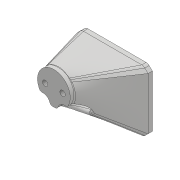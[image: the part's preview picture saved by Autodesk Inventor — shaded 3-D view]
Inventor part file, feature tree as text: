
AUTODESK INVENTOR PART (.ipt)
format: ipt  version: 2018 (Build 220112000, 112)  size: 1,732,096 bytes
history: native  units: mm
features: sketch x48, extrude x40, projected_geometry x39, fillet x13, hole x12, chamfer x10, plane x2, mirror x1, loft x1, other x1
ambient origin geometry x8: Origin, YZ Plane, XZ Plane, XY Plane, X Axis, Y Axis, Z Axis, Center Point
bodies: Solid1 (feature_tree), Solid2 (feature_tree)
feature tree (167):
  extrude  "Extrusion1"  Depth=45.0mm
  extrude  "Extrusion2"  Depth=2.25mm
  hole  "Hole1"  [1 undecoded]
  hole  "Hole2"  [1 undecoded]
  fillet  "Fillet1"  Radius=14.0mm
  extrude  "Extrusion3"  Depth=18.5mm
  extrude  "Extrusion4"  Depth=10.0mm
  extrude  "Extrusion5"  Depth=2.195mm
  extrude  "Extrusion6"  Depth=20.5mm
  hole  "Hole3"  [1 undecoded]
  extrude  "Extrusion7"  Depth=0.5mm
  extrude  "Extrusion8"  Depth=5.0mm TaperAngle=0.0deg
  extrude  "Extrusion9"  Depth=10.0mm
  extrude  "Extrusion10"  Depth=10.0mm
  extrude  "Extrusion11"  Depth=14.5mm
  extrude  "Extrusion12"  Depth=14.5mm
  extrude  "Extrusion13"  Depth=5.0mm
  extrude  "Extrusion14"  Depth=2.25mm
  extrude  "Extrusion15"  Depth=5.0mm
  extrude  "Extrusion16"  Depth=9.0mm
  extrude  "Extrusion17"  Depth=4.0mm
  chamfer  "Chamfer1"  Distance=1.0mm
  fillet  "Fillet7"  Radius=20.7mm
  fillet  "Fillet8"  Radius=32.0mm
  mirror  "Mirror1"
  extrude  "Extrusion19"  Depth=1.0mm TaperAngle=0.0deg
  extrude  "Extrusion20"  Depth=8.0mm
  extrude  "Extrusion21"  Depth=0.2mm TaperAngle=0.0deg
  extrude  "Extrusion22"  Depth=0.5mm TaperAngle=0.0deg
  sketch  "Sketch29"  dims[d77=12.25mm d78=0.0mm d80=8.0mm]
  extrude  "Extrusion23"  Depth=5.0mm TaperAngle=0.0deg
  extrude  "Extrusion24"  Depth=0.2mm TaperAngle=0.0deg
  plane  "Work Plane1"
  extrude  "Extrusion25"  Depth=2.5mm TaperAngle=45.0deg
  extrude  "Extrusion26"  Depth=0.5mm
  extrude  "Extrusion27"  Depth=8.0mm
  extrude  "Extrusion28"  Depth=3.0mm TaperAngle=0.0deg
  extrude  "Extrusion29"  Depth=33.0mm
  extrude  "Extrusion30"  Depth=56.0mm
  extrude  "Extrusion31"  Depth=25.0mm TaperAngle=0.0deg
  chamfer  "Chamfer2"  Distance=6.0mm
  hole  "Hole6"  [1 undecoded]
  chamfer  "Chamfer3"  Distance=40.0mm
  extrude  "Extrusion32"  Depth=12.0mm
  extrude  "Extrusion33"  Depth=40.0mm TaperAngle=0.0deg
  chamfer  "Chamfer4"  Distance=40.0mm
  chamfer  "Chamfer5"  Distance=1.8mm
  chamfer  "Chamfer6"  Distance=3.3mm
  fillet  "Fillet9"  Radius=14.0mm
  extrude  "Extrusion34"  Depth=1.2mm TaperAngle=45.0deg
  chamfer  "Chamfer7"  Distance=2.5mm
  sketch  "Sketch42"  dims[d146=6.0mm d147=0.0mm d149=42.0mm]
  hole  "Hole7"  [1 undecoded]
  hole  "Hole8"  [1 undecoded]
  hole  "Hole9"  [1 undecoded]
  fillet  "Fillet10"  Radius=3.0mm
  chamfer  "Chamfer8"  Distance=2.0mm
  chamfer  "Chamfer9"  Distance=12.0mm
  fillet  "Fillet11"  Radius=2.0mm
  fillet  "Fillet12"  Radius=15.0mm
  extrude  "Extrusion35"  Depth=10.0mm TaperAngle=0.0deg
  sketch  "Sketch45"  dims[d151=4.5mm]
  hole  "Hole10"  [1 undecoded]
  hole  "Hole11"  [1 undecoded]
  hole  "Hole12"  [1 undecoded]
  fillet  "Fillet13"  Radius=3.18mm
  fillet  "Fillet14"  Radius=3.18mm
  fillet  "Fillet15"  Radius=0.5mm
  chamfer  "Chamfer10"  Distance=2.0mm Angle=45.0deg
  extrude  "Extrusion36"  Depth=10.0mm TaperAngle=45.0deg
  sketch  "Sketch47"  dims[d155=28.0mm d156=12.0mm]
  extrude  "Extrusion37"  Depth=10.0mm
  extrude  "Extrusion38"  Depth=10.0mm
  plane  "Work Plane2"
  loft  "Loft1"
  hole  "Hole13"  [1 undecoded]
  extrude  "Extrusion39"  Depth=10.0mm TaperAngle=0.0deg
  extrude  "Extrusion40"  Depth=10.0mm
  fillet  "Fillet16"  Radius=2.75mm
  fillet  "Fillet17"  Radius=2.5mm
  extrude  "Extrusion41"  Depth=10.0mm
  fillet  "Fillet18"  Radius=2.0mm
  hole  "Hole14"  [1 undecoded]
  sketch  "Sketch1"  dims[d0=24.5mm d1=45.0mm]
  sketch  "Sketch2"  dims[d2=1.95mm d3=0.0mm d4=2.25mm]
  projected_geometry  "Projected Loop1"
  sketch  "Sketch3"  dims[d5=20.0mm d6=2.25mm]
  projected_geometry  "Projected Loop2"
  sketch  "Sketch4"  dims[d7=5.25mm d8=5.25mm d9=14.0mm]
  projected_geometry  "Projected Loop3"
  sketch  "Sketch5"  dims[d10=5.25mm d11=18.5mm]
  projected_geometry  "Projected Loop4"
  sketch  "Sketch6"  dims[d12=10.0mm d13=0.0mm d14=20.5mm]
  projected_geometry  "Projected Loop5"
  sketch  "Sketch7"  dims[d15=2.0mm d16=2.195mm]
  projected_geometry  "Projected Loop6"
  sketch  "Sketch8"  dims[d17=2.0mm]
  projected_geometry  "Projected Loop7"
  sketch  "Sketch9"  dims[d18=2.4mm d19=6.0mm d20=4.4mm d21=2.0mm d22=90.0deg d23=8.0mm d24=20.594885mm d25=20.5mm]
  projected_geometry  "Projected Loop8"
  projected_geometry  "Projected Loop9"
  sketch  "Sketch10"  dims[d26=26.65mm d27=2.0mm]
  projected_geometry  "Projected Loop10"
  projected_geometry  "Projected Loop11"
  sketch  "Sketch11"  dims[d28=2.0mm]
  projected_geometry  "Projected Loop12"
  sketch  "Sketch12"  dims[d29=2.4mm d30=6.0mm d31=4.4mm d32=2.0mm d33=90.0deg d34=8.0mm d35=20.594885mm d36=0.5mm]
  sketch  "Sketch13"  dims[d37=18.0mm d38=5.0mm d39=0.0mm]
  sketch  "Sketch14"  dims[d41=10.0mm d42=0.0mm d43=24.5mm]
  projected_geometry  "Projected Loop13"
  sketch  "Sketch15"  dims[d44=1.15mm d45=0.0mm d46=10.0mm]
  sketch  "Sketch16"  dims[d47=21.0mm d48=14.5mm]
  projected_geometry  "Projected Loop14"
  sketch  "Sketch17"  dims[d49=20.0mm d50=14.5mm]
  projected_geometry  "Projected Loop15"
  sketch  "Sketch18"  dims[d51=24.5mm d52=5.0mm]
  projected_geometry  "Projected Loop16"
  sketch  "Sketch19"  dims[d53=5.0mm d54=2.25mm]
  projected_geometry  "Projected Loop17"
  sketch  "Sketch20"  dims[d55=2.25mm d56=5.0mm]
  projected_geometry  "Projected Loop18"
  sketch  "Sketch25"  dims[d57=5.0mm d58=9.0mm]
  projected_geometry  "Projected Loop22"
  sketch  "Sketch26"  dims[d59=14.75mm d60=4.0mm d61=1.0mm d62=0.0mm d63=20.7mm]
  sketch  "Sketch27"  dims[d64=2.4mm d65=6.0mm d66=4.4mm d67=2.0mm d68=90.0deg d69=8.0mm d70=20.594885mm d72=32.0mm]
  projected_geometry  "Projected Loop23"
  sketch  "Sketch28"  dims[d73=5.0mm d74=0.0mm d75=1.0mm d76=0.0mm]
  projected_geometry  "Projected Loop24"
  sketch  "Sketch31"  dims[d81=4.5mm d82=0.0mm d84=0.2mm d85=0.0mm]
  projected_geometry  "Projected Loop25"
  sketch  "Sketch32"  dims[d86=21.0mm d87=0.5mm d88=0.0mm]
  projected_geometry  "Projected Loop26"
  sketch  "Sketch33"  dims[d91=8.0mm d92=0.0mm d93=5.0mm d94=0.0mm]
  sketch  "Sketch34"  dims[d95=5.0mm d96=0.0mm d98=0.2mm d99=0.0mm]
  sketch  "Sketch35"  dims[d100=0.2mm d101=0.0mm d102=2.5mm d103=2.0mm d104=45.0deg]
  projected_geometry  "Projected Loop27"
  sketch  "Sketch36"  dims[d105=1.5mm d114=0.5mm]
  sketch  "Sketch37"  dims[d128=4.0mm d129=0.0mm d130=8.0mm]
  sketch  "Sketch38"  dims[d131=3.0mm d132=0.0mm d133=3.0mm d134=0.0mm]
  projected_geometry  "Projected Loop28"
  sketch  "Sketch39"  dims[d135=25.0mm d136=0.0mm d137=33.0mm]
  projected_geometry  "Projected Loop29"
  sketch  "Sketch40"  dims[d138=2.5mm d139=56.0mm]
  projected_geometry  "Projected Loop30"
  sketch  "Sketch41"  dims[d140=25.0mm d141=0.0mm d142=25.0mm d143=0.0mm d144=6.0mm d145=0.0mm]
  sketch  "Sketch44"  dims[d150=4.5mm]
  projected_geometry  "Projected Loop31"
  projected_geometry  "Projected Loop32"
  projected_geometry  "Projected Loop33"
  sketch  "Sketch46"  dims[d152=4.5mm d153=40.0mm d154=0.0mm]
  projected_geometry  "Projected Loop34"
  sketch  "Sketch48"  dims[d157=12.0mm d158=40.0mm d159=0.0mm d160=40.0mm d161=0.0mm]
  projected_geometry  "Projected Loop35"
  sketch  "Sketch49"  dims[d162=20.5mm d163=1.8mm d164=0.0mm]
  other  "Edges1"
  sketch  "Sketch50"  dims[d165=20.5mm d166=3.3mm d167=0.0mm]
  projected_geometry  "Projected Loop36"
  sketch  "Sketch51"  dims[d168=2.0mm d169=2.0mm d170=45.0deg d171=14.0mm]
  projected_geometry  "Projected Loop37"
  sketch  "Sketch52"  dims[d172=3.1mm d173=6.0mm d174=6.3mm d175=2.0mm d176=90.0deg d177=8.0mm d178=20.594885mm d179=1.2mm d180=2.0mm d181=45.0deg]
  projected_geometry  "Projected Loop38"
  sketch  "Sketch53"  dims[d182=7.0mm d183=2.5mm d184=0.0mm]
  projected_geometry  "Projected Loop39"
  sketch  "Sketch54"  dims[d185=7.0mm d186=2.5mm d187=0.0mm d188=3.0mm d189=15.0mm d190=45.0deg d191=3.0mm d192=15.0mm d193=45.0deg d194=3.0mm d195=15.0mm d196=45.0deg d197=2.0mm d198=12.0mm d199=2.0mm d200=15.0mm d201=20.0mm d202=0.0mm d203=2.0mm d204=15.0mm d205=45.0deg d206=2.9mm d207=2.9mm d208=3.18mm d209=3.18mm d210=4.0mm d211=6.0mm d212=6.3mm d213=2.0mm d214=90.0deg d215=8.0mm d216=20.594885mm d217=1.567mm d218=25.0mm d219=6.3mm d220=2.0mm d221=90.0deg d222=25.0mm d223=20.594885mm d224=2.15mm d225=20.0mm d226=4.4mm d227=2.0mm d228=90.0deg d229=10.0mm d230=0.0mm d231=0.5mm d232=2.0mm d233=15.0mm d234=45.0deg d235=2.0mm d236=15.0mm d237=45.0deg d238=1.0mm d239=3.0mm d240=3.9mm d241=3.9mm d242=3.5mm d243=0.0mm d244=2.75mm d245=2.75mm d246=2.5mm d247=1.567mm d248=4.0mm d249=4.4mm d250=2.0mm d251=90.0deg d252=40.0mm d253=20.594885mm d254=2.1mm d255=4.0mm d256=4.4mm d257=2.0mm d258=90.0deg d259=28.25mm d260=0.0mm d261=3.9mm d262=4.0mm d263=4.4mm d264=2.0mm d265=90.0deg d266=20.0mm d267=0.0mm d268=0.2mm d269=2.0mm d270=2.0mm d271=1.8mm d272=15.0mm d273=45.0deg d274=2.0mm d275=0.0mm d276=20.0mm d277=4.2mm d278=0.0mm d279=5.0mm d280=0.0mm d281=25.0mm d282=15.0mm d283=0.0mm d284=90.0deg d285=0.0mm d286=90.0deg d287=14.0mm d288=9.899495mm d289=9.899495mm d290=3.3mm d291=6.0mm d292=6.3mm d293=2.0mm d294=90.0deg d295=8.0mm d296=20.594885mm d297=7.0mm d298=3.0mm d299=0.0mm d300=6.5mm d301=6.5mm d302=6.5mm d303=6.5mm d304=23.0mm d305=0.0mm d306=1.0mm d307=1.0mm d308=2.0mm d309=0.0mm d310=2.0mm d311=8.0mm d312=2.459mm d313=15.0mm d314=6.3mm d315=2.0mm d316=90.0deg d317=15.0mm d318=20.594885mm]
  projected_geometry  "Project Cut Edges1"
  projected_geometry  "Project Cut Edges2"
  projected_geometry  "Project Cut Edges3"
note: 12 required parameter values undecoded (feature->parameter linkage not recoverable at this tier; creation-order binding heuristic only, values carry confidence <= 0.55)
